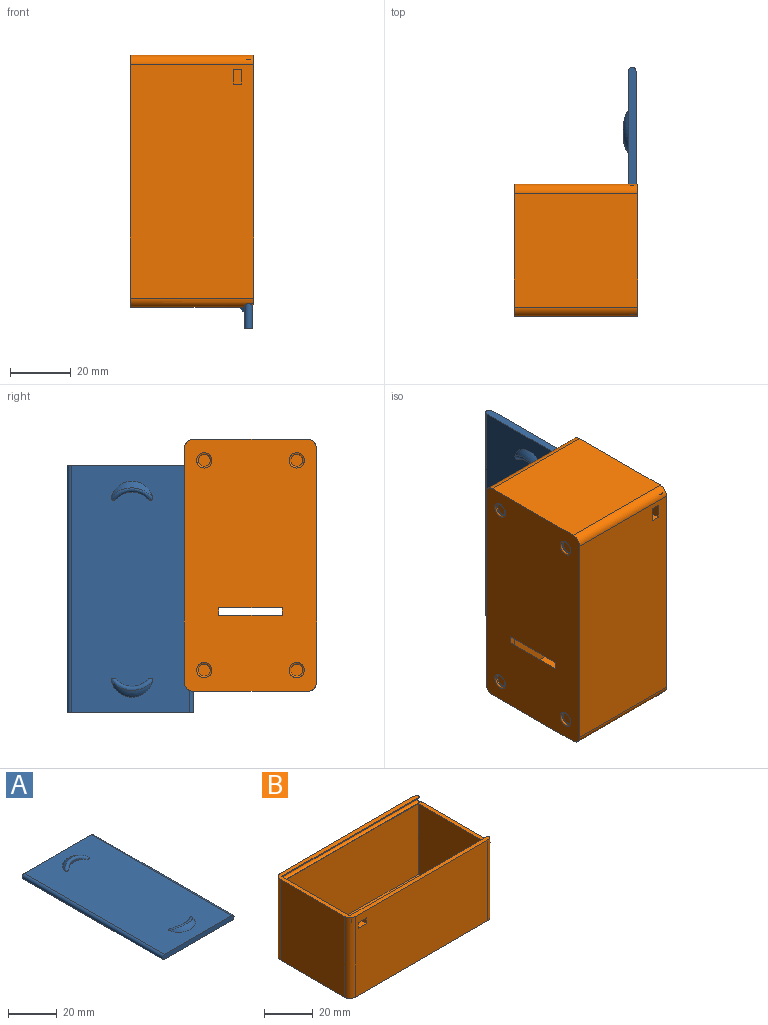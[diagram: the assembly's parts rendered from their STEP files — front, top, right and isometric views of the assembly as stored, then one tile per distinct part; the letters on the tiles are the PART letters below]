
ASSEMBLY  parts=2 mates=1
PART A: 12 faces, bbox 61.5x101.4x30.2 mm
  f0: plane 101.4x59mm, normal (0,0,1), area 3082.5mm2, adj f1,f2,f4,f5,f6,f7,f8,f9
  f1: cylinder r=1.25mm len=81.4mm, axis (0,1,0), area 319.7mm2, adj f0,f3,f4,f5
  f2: cylinder r=1.25mm len=81.4mm, axis (0,1,0), area 319.7mm2, adj f0,f3,f4,f5
  f3: plane 81.4x39mm, normal (0,0,-1), area 3174.6mm2, adj f1,f2,f4,f5
  f4: plane 41.5x2.5mm, normal (0,-1,0), area 102.4mm2, adj f0,f1,f2,f3
  f5: plane 41.5x2.5mm, normal (0,1,0), area 102.4mm2, adj f0,f1,f2,f3
  f6: cylinder r=6.73mm len=8.74mm, axis (0,0,-1), area 0mm2, adj f0,f10
  f7: cylinder r=6.73mm len=8.74mm, axis (0,0,-1), area 0mm2, adj f0,f11
  f8: torus R=2.96mm, axis (0,0,-1), area 0mm2, adj f0,f11
  f9: torus R=2.96mm, axis (0,0,-1), area 0mm2, adj f0,f10
  f10: bspline ~13.82x5.1mm, area 25.9mm2, adj f0,f6,f9
  f11: bspline ~13.82x5.1mm, area 25.9mm2, adj f0,f7,f8
PART B: 68 faces, bbox 83x43.5x40.5 mm
  f0: plane 77x40.5mm, normal (0,1,0), area 3055mm2, adj f2,f4,f5,f28,f52,f53,f54,f55
  f1: plane 79x35.5mm, normal (0,-1,0), area 2741mm2, adj f3,f15,f16,f31,f52,f53,f54,f55
  f2: plane 83x43.5mm, normal (0,0,-1), area 3471.7mm2, adj f0,f4,f7,f11,f13,f14,f28,f29
  f3: plane 79x39.5mm, normal (0,0,1), area 2880.2mm2, adj f1,f12,f15,f16,f36,f37,f38,f39
  f4: cylinder r=3mm len=40.5mm, axis (0,0,1), area 182.6mm2, adj f0,f2,f5,f7,f31,f32,f34
  f5: plane 82.07x43.5mm, normal (0,0,1), area 402mm2, adj f0,f4,f8,f9,f10,f11,f13,f14
  f6: plane 80.35x40mm, normal (0,0,-1), area 59.8mm2, adj f8,f9,f10,f30,f32,f33,f34,f35
  f7: plane 37.5x37.5mm, normal (1,0,0), area 1406.2mm2, adj f2,f4,f11,f31
  f8: plane 79.27x0.5mm, normal (0,1,0), area 39.6mm2, adj f5,f6,f10,f35
  f9: plane 79.27x0.5mm, normal (0,-1,0), area 39.6mm2, adj f5,f6,f10,f34
  f10: plane 39.5x0.5mm, normal (1,0,0), area 19.8mm2, adj f5,f6,f8,f9
  f11: cylinder r=3mm len=40.5mm, axis (0,0,-1), area 182.6mm2, adj f2,f5,f7,f14,f30,f31,f35
  f12: plane 79x35.5mm, normal (0,1,0), area 2780.2mm2, adj f3,f15,f16,f17,f19,f21,f22,f24
  f13: plane 40.5x37.5mm, normal (-1,0,0), area 1518.7mm2, adj f2,f5,f28,f29
  f14: plane 77x40.5mm, normal (0,-1,0), area 3105.1mm2, adj f2,f5,f11,f17,f18,f19,f20,f29
  f15: plane 39.5x35.5mm, normal (1,0,0), area 1402.2mm2, adj f1,f3,f12,f31
  f16: plane 39.5x35.5mm, normal (-1,0,0), area 1402.2mm2, adj f1,f3,f12,f31
  f17: plane 2.8x2mm, normal (1,0,0), area 5.6mm2, adj f12,f14,f18,f20
  f18: plane 4.8x4mm, normal (0,0,1), area 19.2mm2, adj f14,f17,f19,f24,f25,f27
  f19: plane 2.8x2mm, normal (-1,0,0), area 5.6mm2, adj f12,f14,f18,f20
  f20: plane 4.8x4mm, normal (0,0,-1), area 19.2mm2, adj f14,f17,f19,f21,f22,f23
  f21: plane 2x0.88mm, normal (-1,0,0), area 1.8mm2, adj f12,f20,f23,f31
  f22: plane 2x0.88mm, normal (1,0,0), area 1.8mm2, adj f12,f20,f23,f31
  f23: plane 4.8x0.88mm, normal (0,1,0), area 4.2mm2, adj f20,f21,f22,f31
  f24: plane 2x1.38mm, normal (-1,0,0), area 2.8mm2, adj f12,f18,f26,f27
  f25: plane 2x1.38mm, normal (1,0,0), area 2.8mm2, adj f12,f18,f26,f27
  f26: plane 4.8x2mm, normal (0,0,-1), area 9.6mm2, adj f12,f24,f25,f27
  f27: plane 4.8x1.38mm, normal (0,1,0), area 6.6mm2, adj f18,f24,f25,f26
  f28: cylinder r=3mm len=40.5mm, axis (0,0,-1), area 190.9mm2, adj f0,f2,f5,f13
  f29: cylinder r=3mm len=40.5mm, axis (0,0,1), area 190.9mm2, adj f2,f5,f13,f14
  f30: cylinder r=1.25mm len=81.23mm, axis (1,0,0), area 316.2mm2, adj f6,f11,f31,f33,f35
  f31: plane 81.5x40mm, normal (0,0,1), area 148.9mm2, adj f1,f4,f7,f11,f12,f15,f16,f21
  f32: cylinder r=1.25mm len=81.23mm, axis (1,0,0), area 316.2mm2, adj f4,f6,f31,f33,f34
  f33: plane 42.5x2.5mm, normal (1,0,0), area 104.9mm2, adj f6,f30,f31,f32
  f34: cylinder r=0.8mm len=1.45mm, axis (0,0,1), area 1.4mm2, adj f4,f5,f6,f9,f32
  f35: cylinder r=0.8mm len=1.45mm, axis (0,0,-1), area 1.4mm2, adj f5,f6,f8,f11,f30
  f36: plane 11.44x2mm, normal (0,1,0), area 10.5mm2, adj f2,f3,f38,f39
  f37: plane 11.44x2mm, normal (0,-1,0), area 10.5mm2, adj f2,f3,f38,f39
  f38: cylinder r=6mm len=21mm, axis (0,1,0), area 106mm2, adj f2,f3,f36,f37
  f39: cylinder r=6mm len=21mm, axis (0,1,0), area 106mm2, adj f2,f3,f36,f37
  f40: cylinder r=2mm len=4mm, axis (0,0,-1), area 6.3mm2, adj f41,f51
  f41: plane 4x4mm, normal (0,0,-1), area 12.6mm2, adj f40
  f42: cylinder r=2mm len=4mm, axis (0,0,-1), area 6.3mm2, adj f43,f50
  f43: plane 4x4mm, normal (0,0,-1), area 12.6mm2, adj f42
  f44: cylinder r=2mm len=4mm, axis (0,0,-1), area 6.3mm2, adj f45,f49
  f45: plane 4x4mm, normal (0,0,-1), area 12.6mm2, adj f44
  f46: cylinder r=2mm len=4mm, axis (0,0,-1), area 6.3mm2, adj f47,f48
  f47: plane 4x4mm, normal (0,0,-1), area 12.6mm2, adj f46
  f48: torus R=2.5mm, axis (0,0,1), area 10.8mm2, adj f2,f46
  f49: torus R=2.5mm, axis (0,0,1), area 10.8mm2, adj f2,f44
  f50: torus R=2.5mm, axis (0,0,1), area 10.8mm2, adj f2,f42
  f51: torus R=2.5mm, axis (0,0,1), area 10.8mm2, adj f2,f40
  f52: plane 2x1.74mm, normal (1,0,0), area 3.5mm2, adj f0,f1,f53,f55
  f53: plane 15x15mm, normal (-0.71,0,-0.71), area 42.4mm2, adj f0,f1,f52,f54
  f54: plane 2x1.74mm, normal (0,0,1), area 3.5mm2, adj f0,f1,f53,f55
  f55: plane 13.27x13.27mm, normal (0.71,0,0.71), area 37.5mm2, adj f0,f1,f52,f54
  f56: plane 2x1.85mm, normal (1,0,0), area 3.7mm2, adj f0,f1,f57,f59
  f57: plane 2.8x2.8mm, normal (-0.71,0,-0.71), area 7.9mm2, adj f0,f1,f56,f58
  f58: plane 2x1.84mm, normal (0,0,1), area 3.7mm2, adj f0,f1,f57,f59
  f59: plane 2x0.95mm, normal (0.71,0,0.71), area 2.7mm2, adj f0,f1,f56,f58
  f60: plane 2x1.97mm, normal (1,0,0), area 3.9mm2, adj f0,f1,f61,f63
  f61: plane 11.81x11.81mm, normal (-0.71,0,-0.71), area 33.4mm2, adj f0,f1,f60,f62
  f62: plane 2x1.97mm, normal (0,0,1), area 3.9mm2, adj f0,f1,f61,f63
  f63: plane 9.85x9.85mm, normal (0.71,0,0.71), area 27.8mm2, adj f0,f1,f60,f62
  f64: plane 2.21x2mm, normal (1,0,0), area 4.4mm2, adj f0,f1,f65,f67
  f65: plane 7.5x7.5mm, normal (-0.71,0,-0.71), area 21.2mm2, adj f0,f1,f64,f66
  f66: plane 2.21x2mm, normal (0,0,1), area 4.4mm2, adj f0,f1,f65,f67
  f67: plane 5.29x5.29mm, normal (0.71,0,0.71), area 14.9mm2, adj f0,f1,f64,f66
PLACE A rot(axis=(0.58,-0.58,-0.58),120deg) t=(-8.91,-12.59,72.36)mm
PLACE B rot(axis=(0,1,0),90deg) t=(-7.16,-51.59,39.52)mm
MATE slider A.f1 <-> B.f32  axis (0,0,1) through (-8.91,-31.59,72.36)mm
